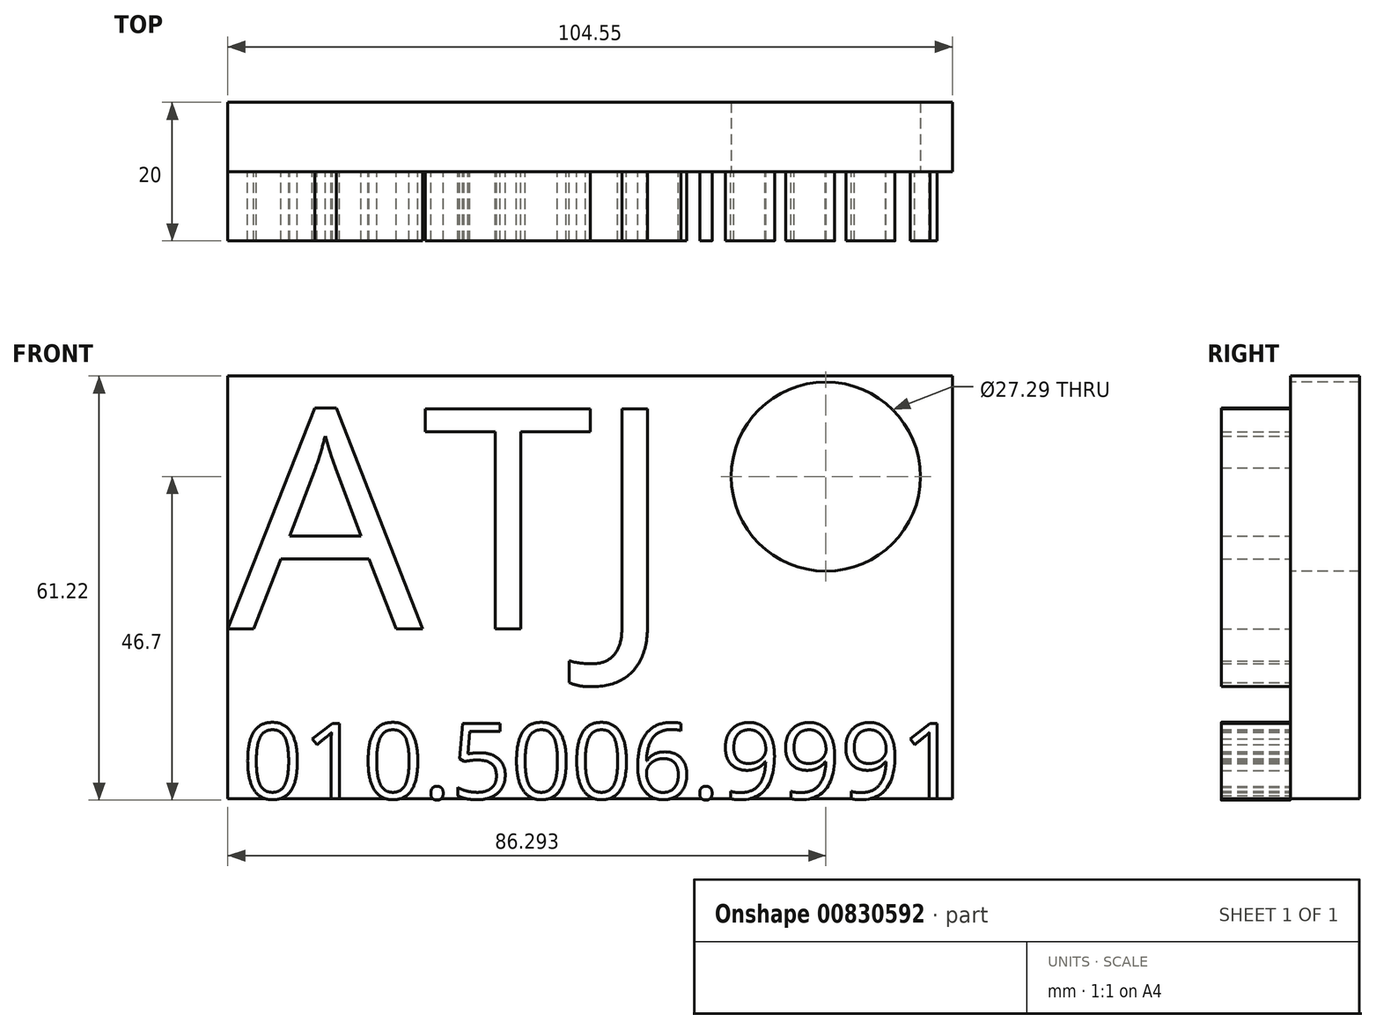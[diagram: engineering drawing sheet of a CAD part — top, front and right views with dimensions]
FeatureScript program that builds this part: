
annotation { "Feature Type Name" : "Feature", "Feature Type Description" : "" }
export const myFeature = defineFeature(function(context is Context, id is Id, definition is map)
    precondition{}
    {
        {
            var Q0;
            Q0=qCreatedBy(makeId("Front.planeOp"),FACE);
            var sketch = newSketch(context, id + "F0", { "sketchPlane" : qUnion([Q0])});
            skLineSegment(sketch, "E0.bottom", {"start": v(0, 0) * mm, "end": v(104.55, 0) * mm});
            skLineSegment(sketch, "E0.top", {"start": v(0, 61) * mm, "end": v(104.55, 61) * mm});
            skLineSegment(sketch, "E0.left", {"start": v(0, 0) * mm, "end": v(0, 61) * mm});
            skLineSegment(sketch, "E0.right", {"start": v(104.55, 0) * mm, "end": v(104.55, 61) * mm});
            skSolve(sketch);
        }
        {
            var Q0;
            Q0=makeQuery(id+"F0.imprint","IMPRINT",FACE,{"disambiguationData":[TD([[makeQuery(id+"F0.imprint","IMPRINT",EDGE,{"derivedFrom":sQuery(id+"F0.wireOp",EDGE,"E0.bottom")}),1.0]])]});
            extrude(context, id + "F1", {"entities" : qUnion([Q0]), "depth" : 10 * mm, "offsetDistance" : 25.4 * mm});
        }
        {
            var Q0;
            Q0=makeQuery(id+"F1.opExtrude","CAP_FACE",FACE,{"disambiguationData":[OSD([sQuery(id+"F0.wireOp",EDGE,"E0.bottom"),sQuery(id+"F0.wireOp",EDGE,"E0.top"),sQuery(id+"F0.wireOp",EDGE,"E0.left"),sQuery(id+"F0.wireOp",EDGE,"E0.right")])],"isStart":false});
            var sketch = newSketch(context, id + "F2", { "sketchPlane" : qUnion([Q0])});
            skText(sketch, "E1", { "text": "ATJ", "fontName": "OpenSans-Regular.ttf"});
            const initialGuessF2  = {"E1": [0, 0.02452, 1, 0, 0.03201]};
            skSetInitialGuess(sketch, initialGuessF2);
            skSolve(sketch);
        }
        {
            var Q0;
            Q0 = qSketchRegion(id + "F2", true);
            extrude(context, id + "F3", {"entities" : qUnion([Q0]), "operationType" : NewBodyOperationType.ADD, "depth" : 10 * mm, "offsetDistance" : 25.4 * mm});
        }
        {
            var Q0;
            {var subQ0=sQuery(id+"F0.wireOp",EDGE,"E0.top");var subQ1=sQuery(id+"F0.wireOp",EDGE,"E0.right");var subQ2=sQuery(id+"F0.wireOp",EDGE,"E0.bottom");var subQ3=sQuery(id+"F0.wireOp",EDGE,"E0.left");Q0=makeQuery(id+"F3.boolean.opBoolean","SPLIT",FACE,{"disambiguationData":[TD([makeQuery(id+"F1.opExtrude","SWEPT_FACE",FACE,{"disambiguationData":[OSD([subQ2])]})])],"derivedFrom":makeQuery(id+"F1.opExtrude","CAP_FACE",FACE,{"disambiguationData":[OSD([subQ2,subQ0,subQ3,subQ1])],"isStart":false})});}
            var sketch = newSketch(context, id + "F4", { "sketchPlane" : qUnion([Q0])});
            skText(sketch, "E2", { "text": "010.5006.9991", "fontName": "OpenSans-Regular.ttf"});
            const initialGuessF4  = {"E2": [0.00211, 0, 1, 0, 0.01094]};
            skSetInitialGuess(sketch, initialGuessF4);
            skSolve(sketch);
        }
        {
            var Q0;
            Q0 = qSketchRegion(id + "F4", true);
            extrude(context, id + "F5", {"entities" : qUnion([Q0]), "operationType" : NewBodyOperationType.ADD, "depth" : 10 * mm, "offsetDistance" : 25.4 * mm});
        }
        {
            var Q0;
            {var subQ55=sQuery(id+"F0.wireOp",EDGE,"E0.top");var subQ57=sQuery(id+"F0.wireOp",EDGE,"E0.right");var subQ65=sQuery(id+"F0.wireOp",EDGE,"E0.bottom");var subQ66=makeQuery(id+"F1.opExtrude","SWEPT_FACE",FACE,{"disambiguationData":[OSD([subQ65])]});var subQ70=sQuery(id+"F0.wireOp",EDGE,"E0.left");Q0=makeQuery(id+"F5.boolean.opBoolean","SPLIT",FACE,{"disambiguationData":[TD([subQ66])],"derivedFrom":makeQuery(id+"F3.boolean.opBoolean","SPLIT",FACE,{"disambiguationData":[TD([subQ66])],"derivedFrom":makeQuery(id+"F1.opExtrude","CAP_FACE",FACE,{"disambiguationData":[OSD([subQ65,subQ55,subQ70,subQ57])],"isStart":false})})});}
            var sketch = newSketch(context, id + "F6", { "sketchPlane" : qUnion([Q0])});
            skCircle(sketch, "E3", {"center": v(86.3, 46.48) * mm, "radius": 13.65 * mm});
            skSolve(sketch);
        }
        {
            var Q0;
            Q0 = qSketchRegion(id + "F6", true);
            extrude(context, id + "F7", {"entities" : qUnion([Q0]), "operationType" : NewBodyOperationType.REMOVE, "oppositeDirection" : true, "depth" : 25.4 * mm, "offsetDistance" : 25.4 * mm});
        }
    });
